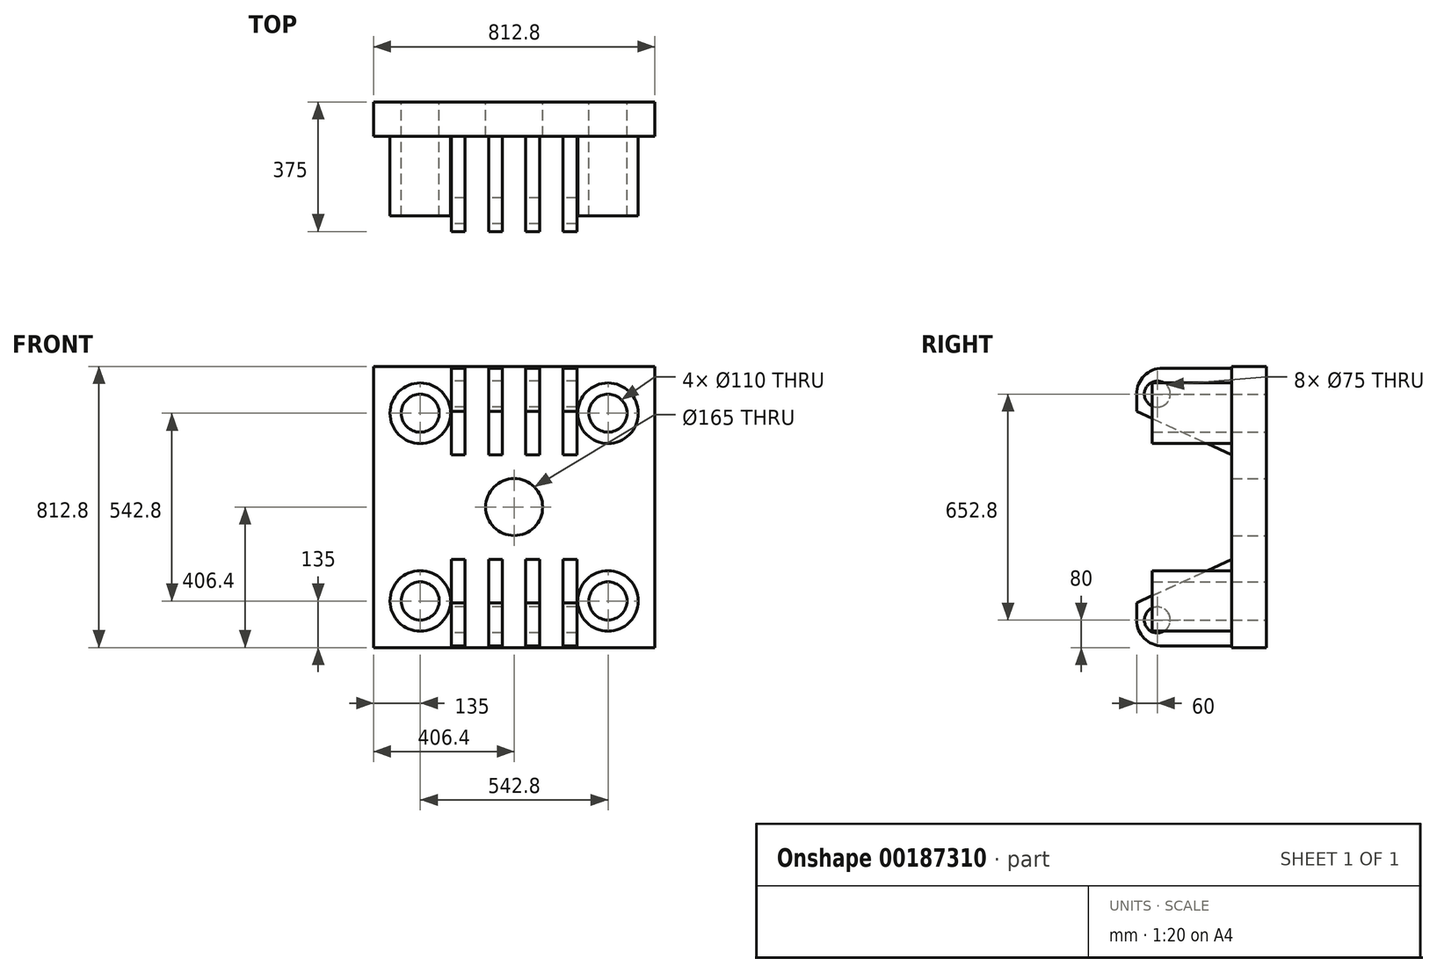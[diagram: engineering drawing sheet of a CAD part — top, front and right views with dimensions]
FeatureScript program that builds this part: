
annotation { "Feature Type Name" : "Feature", "Feature Type Description" : "" }
export const myFeature = defineFeature(function(context is Context, id is Id, definition is map)
    precondition{}
    {
        {
            var Q0;
            Q0=qCreatedBy(makeId("Front.planeOp"),FACE);
            var sketch = newSketch(context, id + "F0", { "sketchPlane" : qUnion([Q0])});
            skLineSegment(sketch, "E0.bottom", {"start": v(-406.4, -406.4) * mm, "end": v(406.4, -406.4) * mm});
            skLineSegment(sketch, "E0.top", {"start": v(-406.4, 406.4) * mm, "end": v(406.4, 406.4) * mm});
            skLineSegment(sketch, "E0.left", {"start": v(-406.4, -406.4) * mm, "end": v(-406.4, 406.4) * mm});
            skLineSegment(sketch, "E0.right", {"start": v(406.4, -406.4) * mm, "end": v(406.4, 406.4) * mm});
            skPoint(sketch, "E0.middle", {"position": v(0, 0) * mm});
            skLineSegment(sketch, "E1", {"start": v(-271.4, 435.08) * mm, "end": v(-271.4, -466.79) * mm, "construction": true});
            skLineSegment(sketch, "E2", {"start": v(271.4, 435.63) * mm, "end": v(271.4, -467.34) * mm, "construction": true});
            skLineSegment(sketch, "E3", {"start": v(-482.99, 271.4) * mm, "end": v(474.5, 271.4) * mm, "construction": true});
            skLineSegment(sketch, "E4", {"start": v(-470.32, -271.4) * mm, "end": v(478.3, -271.4) * mm, "construction": true});
            skCircle(sketch, "E5", {"center": v(-271.4, 271.4) * mm, "radius": 55 * mm});
            skLineSegment(sketch, "E6", {"start": v(-420.18, 0) * mm, "end": v(457.83, 0) * mm, "construction": true});
            skCircle(sketch, "E7.MirrorC", {"center": v(-271.4, -271.4) * mm, "radius": 55 * mm});
            skLineSegment(sketch, "E8", {"start": v(0, 436.93) * mm, "end": v(0, -451.52) * mm, "construction": true});
            skCircle(sketch, "E9.MirrorC", {"center": v(271.4, -271.4) * mm, "radius": 55 * mm});
            skCircle(sketch, "E10.MirrorC", {"center": v(271.4, 271.4) * mm, "radius": 55 * mm});
            skCircle(sketch, "E11", {"center": v(0, 0) * mm, "radius": 82.5 * mm});
            skSolve(sketch);
        }
        {
            var Q0;
            Q0=qSketchRegion(id+"F0",true);
            extrude(context, id + "F1", {"entities" : qUnion([Q0]), "depth" : 100 * mm});
        }
        {
            var Q0;
            Q0=makeQuery(id+"F1.opExtrude","CAP_FACE",FACE,{"disambiguationData":[OSD([sQuery(id+"F0.wireOp",EDGE,"E0.bottom"),sQuery(id+"F0.wireOp",EDGE,"E0.top"),sQuery(id+"F0.wireOp",EDGE,"E0.left"),sQuery(id+"F0.wireOp",EDGE,"E0.right"),sQuery(id+"F0.wireOp",EDGE,"E5"),sQuery(id+"F0.wireOp",EDGE,"E7.MirrorC"),sQuery(id+"F0.wireOp",EDGE,"E9.MirrorC"),sQuery(id+"F0.wireOp",EDGE,"E10.MirrorC"),sQuery(id+"F0.wireOp",EDGE,"E11")])],"isStart":false});
            var sketch = newSketch(context, id + "F2", { "sketchPlane" : qUnion([Q0])});
            skCircle(sketch, "E12", {"center": v(-271.4, 271.4) * mm, "radius": 87.5 * mm});
            skCircle(sketch, "E13", {"center": v(-271.4, 271.4) * mm, "radius": 55 * mm});
            skCircle(sketch, "E14", {"center": v(271.4, 271.4) * mm, "radius": 87.5 * mm});
            skCircle(sketch, "E15", {"center": v(271.4, 271.4) * mm, "radius": 55 * mm});
            skCircle(sketch, "E16", {"center": v(271.4, -271.4) * mm, "radius": 87.5 * mm});
            skCircle(sketch, "E17", {"center": v(271.4, -271.4) * mm, "radius": 55 * mm});
            skCircle(sketch, "E18", {"center": v(-271.4, -271.4) * mm, "radius": 87.5 * mm});
            skCircle(sketch, "E19", {"center": v(-271.4, -271.4) * mm, "radius": 55 * mm});
            skSolve(sketch);
        }
        {
            var Q0;
            Q0 = qSketchRegion(id + "F2", true);
            extrude(context, id + "F3", {"entities" : qUnion([Q0]), "operationType" : NewBodyOperationType.ADD, "depth" : 230 * mm});
        }
        {
            var Q0;
            Q0=makeQuery(id+"FbqTgrZJ77ltsDz_1.opFillet","SPLIT",FACE,{"disambiguationData":[OD(4.0)],"derivedFrom":makeQuery(id+"F1.opExtrude","CAP_FACE",FACE,{"disambiguationData":[OSD([sQuery(id+"F0.wireOp",EDGE,"E0.bottom"),sQuery(id+"F0.wireOp",EDGE,"E0.top"),sQuery(id+"F0.wireOp",EDGE,"E0.left"),sQuery(id+"F0.wireOp",EDGE,"E0.right"),sQuery(id+"F0.wireOp",EDGE,"E5"),sQuery(id+"F0.wireOp",EDGE,"E7.MirrorC"),sQuery(id+"F0.wireOp",EDGE,"E9.MirrorC"),sQuery(id+"F0.wireOp",EDGE,"E10.MirrorC"),sQuery(id+"F0.wireOp",EDGE,"E11")])],"isStart":false})});
            var sketch = newSketch(context, id + "F4", { "sketchPlane" : qUnion([Q0])});
            skLineSegment(sketch, "E20.bottom", {"start": v(-73.8, 401.4) * mm, "end": v(-33.8, 401.4) * mm});
            skLineSegment(sketch, "E20.top", {"start": v(-73.8, 151.4) * mm, "end": v(-33.8, 151.4) * mm});
            skLineSegment(sketch, "E20.left", {"start": v(-73.8, 401.4) * mm, "end": v(-73.8, 151.4) * mm});
            skLineSegment(sketch, "E20.right", {"start": v(-33.8, 401.4) * mm, "end": v(-33.8, 151.4) * mm});
            skLineSegment(sketch, "E21.bottom", {"start": v(33.8, 401.4) * mm, "end": v(73.8, 401.4) * mm});
            skLineSegment(sketch, "E21.top", {"start": v(33.8, 151.4) * mm, "end": v(73.8, 151.4) * mm});
            skLineSegment(sketch, "E21.left", {"start": v(33.8, 401.4) * mm, "end": v(33.8, 151.4) * mm});
            skLineSegment(sketch, "E21.right", {"start": v(73.8, 401.4) * mm, "end": v(73.8, 151.4) * mm});
            skLineSegment(sketch, "E22.bottom", {"start": v(141.4, 401.4) * mm, "end": v(181.4, 401.4) * mm});
            skLineSegment(sketch, "E22.top", {"start": v(141.4, 151.4) * mm, "end": v(181.4, 151.4) * mm});
            skLineSegment(sketch, "E22.left", {"start": v(141.4, 401.4) * mm, "end": v(141.4, 151.4) * mm});
            skLineSegment(sketch, "E22.right", {"start": v(181.4, 401.4) * mm, "end": v(181.4, 151.4) * mm});
            skLineSegment(sketch, "E23", {"start": v(33.8, 401.4) * mm, "end": v(-33.8, 401.4) * mm, "construction": true});
            skLineSegment(sketch, "E24", {"start": v(73.8, 401.4) * mm, "end": v(141.4, 401.4) * mm, "construction": true});
            skLineSegment(sketch, "E25", {"start": v(-406.4, 0) * mm, "end": v(406.4, 0) * mm, "construction": true});
            skLineSegment(sketch, "E26.MirrorCS", {"start": v(141.4, -401.4) * mm, "end": v(181.4, -401.4) * mm});
            skLineSegment(sketch, "E27.MirrorCS", {"start": v(33.8, -401.4) * mm, "end": v(73.8, -401.4) * mm});
            skLineSegment(sketch, "E28.MirrorCS", {"start": v(-73.8, -401.4) * mm, "end": v(-33.8, -401.4) * mm});
            skLineSegment(sketch, "E29.MirrorCS", {"start": v(-73.8, -151.4) * mm, "end": v(-33.8, -151.4) * mm});
            skLineSegment(sketch, "E30.MirrorCS", {"start": v(141.4, -401.4) * mm, "end": v(141.4, -151.4) * mm});
            skLineSegment(sketch, "E31.MirrorCS", {"start": v(141.4, -151.4) * mm, "end": v(181.4, -151.4) * mm});
            skLineSegment(sketch, "E32.MirrorCS", {"start": v(73.8, -401.4) * mm, "end": v(73.8, -151.4) * mm});
            skLineSegment(sketch, "E33.MirrorCS", {"start": v(33.8, -401.4) * mm, "end": v(33.8, -151.4) * mm});
            skLineSegment(sketch, "E34.MirrorCS", {"start": v(181.4, -401.4) * mm, "end": v(181.4, -151.4) * mm});
            skLineSegment(sketch, "E35.MirrorCS", {"start": v(33.8, -151.4) * mm, "end": v(73.8, -151.4) * mm});
            skLineSegment(sketch, "E36.MirrorCS", {"start": v(-33.8, -401.4) * mm, "end": v(-33.8, -151.4) * mm});
            skLineSegment(sketch, "E37.MirrorCS", {"start": v(-73.8, -401.4) * mm, "end": v(-73.8, -151.4) * mm});
            skLineSegment(sketch, "E38.bottom", {"start": v(-181.4, 401.4) * mm, "end": v(-141.4, 401.4) * mm});
            skLineSegment(sketch, "E38.top", {"start": v(-181.4, 151.4) * mm, "end": v(-141.4, 151.4) * mm});
            skLineSegment(sketch, "E38.left", {"start": v(-181.4, 401.4) * mm, "end": v(-181.4, 151.4) * mm});
            skLineSegment(sketch, "E38.right", {"start": v(-141.4, 401.4) * mm, "end": v(-141.4, 151.4) * mm});
            skLineSegment(sketch, "E39", {"start": v(-73.8, 401.4) * mm, "end": v(-141.4, 401.4) * mm, "construction": true});
            skLineSegment(sketch, "E40.MirrorCS", {"start": v(-181.4, -401.4) * mm, "end": v(-141.4, -401.4) * mm});
            skLineSegment(sketch, "E41.MirrorCS", {"start": v(-181.4, -401.4) * mm, "end": v(-181.4, -151.4) * mm});
            skLineSegment(sketch, "E42.MirrorCS", {"start": v(-141.4, -401.4) * mm, "end": v(-141.4, -151.4) * mm});
            skLineSegment(sketch, "E43.MirrorCS", {"start": v(-181.4, -151.4) * mm, "end": v(-141.4, -151.4) * mm});
            skSolve(sketch);
        }
        {
            var Q0;
            Q0 = qSketchRegion(id + "F4", true);
            extrude(context, id + "F5", {"entities" : qUnion([Q0]), "operationType" : NewBodyOperationType.ADD, "depth" : 275 * mm});
        }
        {
            var Q0;
            Q0=makeQuery(id+"F5.opExtrude","SWEPT_FACE",FACE,{"disambiguationData":[OSD([sQuery(id+"F4.wireOp",EDGE,"E38.left")])]});
            var sketch = newSketch(context, id + "F6", { "sketchPlane" : qUnion([Q0])});
            skLineSegment(sketch, "E44", {"start": v(375, 276.4) * mm, "end": v(100, 151.4) * mm});
            skLineSegment(sketch, "E45", {"start": v(100, 151.4) * mm, "end": v(375, 151.4) * mm});
            skLineSegment(sketch, "E46", {"start": v(375, 151.4) * mm, "end": v(375, 276.4) * mm});
            skLineSegment(sketch, "E47", {"start": v(-96.66, 0) * mm, "end": v(488.13, 0) * mm, "construction": true});
            skLineSegment(sketch, "E48.MirrorCS", {"start": v(100, -151.4) * mm, "end": v(375, -151.4) * mm});
            skLineSegment(sketch, "E49.MirrorCS", {"start": v(375, -151.4) * mm, "end": v(375, -276.4) * mm});
            skLineSegment(sketch, "E50.MirrorCS", {"start": v(375, -276.4) * mm, "end": v(100, -151.4) * mm});
            skSolve(sketch);
        }
        {
            var Q0;
            Q0 = qSketchRegion(id + "F6", true);
            var Q1;
            Q1=makeQuery(id+"F5.opExtrude","SWEPT_FACE",FACE,{"disambiguationData":[OSD([sQuery(id+"F4.wireOp",EDGE,"E22.right")])]});
            extrude(context, id + "F7", {"entities" : qUnion([Q0]), "operationType" : NewBodyOperationType.REMOVE, "endBound" : BoundingType.UP_TO_SURFACE, "oppositeDirection" : true, "endBoundEntityFace" : qUnion([Q1]), "depth" : 25 * mm});
        }
        {
            var Q0;
            Q0=makeQuery(id+"F5.opExtrude","CAP_EDGE",EDGE,{"disambiguationData":[OSD([sQuery(id+"F4.wireOp",EDGE,"E22.bottom")])],"isStart":false});
            var Q1;
            {var subQ1=sQuery(id+"F4.wireOp",EDGE,"E22.left");var subQ2=sQuery(id+"F6.wireOp",EDGE,"E44");Q1=makeQuery(id+"F7.boolean.opBoolean","COPY",EDGE,{"disambiguationData":[TD([makeQuery(id+"F5.opExtrude","SWEPT_FACE",FACE,{"disambiguationData":[OSD([subQ1])]})])],"derivedFrom":makeQuery(id+"F7.opExtrude","SWEPT_EDGE",EDGE,{"disambiguationData":[OSD([sQuery(id+"F4.wireOp",EDGE,"E38.left"),subQ2,sQuery(id+"F6.wireOp",EDGE,"E46")])]})});}
            var Q2;
            Q2=makeQuery(id+"F5.opExtrude","CAP_EDGE",EDGE,{"disambiguationData":[OSD([sQuery(id+"F4.wireOp",EDGE,"E21.bottom")])],"isStart":false});
            var Q3;
            {var subQ1=sQuery(id+"F4.wireOp",EDGE,"E21.left");var subQ2=sQuery(id+"F6.wireOp",EDGE,"E44");Q3=makeQuery(id+"F7.boolean.opBoolean","COPY",EDGE,{"disambiguationData":[TD([makeQuery(id+"F5.opExtrude","SWEPT_FACE",FACE,{"disambiguationData":[OSD([subQ1])]})])],"derivedFrom":makeQuery(id+"F7.opExtrude","SWEPT_EDGE",EDGE,{"disambiguationData":[OSD([sQuery(id+"F4.wireOp",EDGE,"E38.left"),subQ2,sQuery(id+"F6.wireOp",EDGE,"E46")])]})});}
            var Q4;
            Q4=makeQuery(id+"F5.opExtrude","CAP_EDGE",EDGE,{"disambiguationData":[OSD([sQuery(id+"F4.wireOp",EDGE,"E20.bottom")])],"isStart":false});
            var Q5;
            {var subQ1=sQuery(id+"F4.wireOp",EDGE,"E20.left");var subQ2=sQuery(id+"F6.wireOp",EDGE,"E44");Q5=makeQuery(id+"F7.boolean.opBoolean","COPY",EDGE,{"disambiguationData":[TD([makeQuery(id+"F5.opExtrude","SWEPT_FACE",FACE,{"disambiguationData":[OSD([subQ1])]})])],"derivedFrom":makeQuery(id+"F7.opExtrude","SWEPT_EDGE",EDGE,{"disambiguationData":[OSD([sQuery(id+"F4.wireOp",EDGE,"E38.left"),subQ2,sQuery(id+"F6.wireOp",EDGE,"E46")])]})});}
            var Q6;
            Q6=makeQuery(id+"F5.opExtrude","CAP_EDGE",EDGE,{"disambiguationData":[OSD([sQuery(id+"F4.wireOp",EDGE,"E38.bottom")])],"isStart":false});
            var Q7;
            {var subQ1=sQuery(id+"F4.wireOp",EDGE,"E38.left");var subQ2=sQuery(id+"F6.wireOp",EDGE,"E44");Q7=makeQuery(id+"F7.boolean.opBoolean","COPY",EDGE,{"disambiguationData":[TD([makeQuery(id+"F5.opExtrude","SWEPT_FACE",FACE,{"disambiguationData":[OSD([subQ1])]})])],"derivedFrom":makeQuery(id+"F7.opExtrude","SWEPT_EDGE",EDGE,{"disambiguationData":[OSD([subQ1,subQ2,sQuery(id+"F6.wireOp",EDGE,"E46")])]})});}
            var Q8;
            {var subQ1=sQuery(id+"F4.wireOp",EDGE,"E41.MirrorCS");var subQ2=sQuery(id+"F6.wireOp",EDGE,"E50.MirrorCS");Q8=makeQuery(id+"F7.boolean.opBoolean","COPY",EDGE,{"disambiguationData":[TD([makeQuery(id+"F5.opExtrude","SWEPT_FACE",FACE,{"disambiguationData":[OSD([subQ1])]})])],"derivedFrom":makeQuery(id+"F7.opExtrude","SWEPT_EDGE",EDGE,{"disambiguationData":[OSD([sQuery(id+"F6.wireOp",EDGE,"E49.MirrorCS"),subQ2])]})});}
            var Q9;
            Q9=makeQuery(id+"F5.opExtrude","CAP_EDGE",EDGE,{"disambiguationData":[OSD([sQuery(id+"F4.wireOp",EDGE,"E40.MirrorCS")])],"isStart":false});
            var Q10;
            {var subQ1=sQuery(id+"F4.wireOp",EDGE,"E36.MirrorCS");var subQ2=sQuery(id+"F6.wireOp",EDGE,"E50.MirrorCS");Q10=makeQuery(id+"F7.boolean.opBoolean","COPY",EDGE,{"disambiguationData":[TD([makeQuery(id+"F5.opExtrude","SWEPT_FACE",FACE,{"disambiguationData":[OSD([subQ1])]})])],"derivedFrom":makeQuery(id+"F7.opExtrude","SWEPT_EDGE",EDGE,{"disambiguationData":[OSD([sQuery(id+"F6.wireOp",EDGE,"E49.MirrorCS"),subQ2])]})});}
            var Q11;
            Q11=makeQuery(id+"F5.opExtrude","CAP_EDGE",EDGE,{"disambiguationData":[OSD([sQuery(id+"F4.wireOp",EDGE,"E28.MirrorCS")])],"isStart":false});
            var Q12;
            {var subQ1=sQuery(id+"F4.wireOp",EDGE,"E32.MirrorCS");var subQ2=sQuery(id+"F6.wireOp",EDGE,"E50.MirrorCS");Q12=makeQuery(id+"F7.boolean.opBoolean","COPY",EDGE,{"disambiguationData":[TD([makeQuery(id+"F5.opExtrude","SWEPT_FACE",FACE,{"disambiguationData":[OSD([subQ1])]})])],"derivedFrom":makeQuery(id+"F7.opExtrude","SWEPT_EDGE",EDGE,{"disambiguationData":[OSD([sQuery(id+"F6.wireOp",EDGE,"E49.MirrorCS"),subQ2])]})});}
            var Q13;
            Q13=makeQuery(id+"F5.opExtrude","CAP_EDGE",EDGE,{"disambiguationData":[OSD([sQuery(id+"F4.wireOp",EDGE,"E27.MirrorCS")])],"isStart":false});
            var Q14;
            {var subQ1=sQuery(id+"F4.wireOp",EDGE,"E30.MirrorCS");var subQ2=sQuery(id+"F6.wireOp",EDGE,"E50.MirrorCS");Q14=makeQuery(id+"F7.boolean.opBoolean","COPY",EDGE,{"disambiguationData":[TD([makeQuery(id+"F5.opExtrude","SWEPT_FACE",FACE,{"disambiguationData":[OSD([subQ1])]})])],"derivedFrom":makeQuery(id+"F7.opExtrude","SWEPT_EDGE",EDGE,{"disambiguationData":[OSD([sQuery(id+"F6.wireOp",EDGE,"E49.MirrorCS"),subQ2])]})});}
            var Q15;
            Q15=makeQuery(id+"F5.opExtrude","CAP_EDGE",EDGE,{"disambiguationData":[OSD([sQuery(id+"F4.wireOp",EDGE,"E26.MirrorCS")])],"isStart":false});
            fillet(context, id + "F8", {"entities" : qUnion([Q0, Q1, Q2, Q3, Q4, Q5, Q6, Q7, Q8, Q9, Q10, Q11, Q12, Q13, Q14, Q15]), "radius" : 75 * mm, "tangentPropagation" : true, "allowEdgeOverflow" : false});
        }
        {
            var Q0;
            Q0=makeQuery(id+"F5.opExtrude","SWEPT_FACE",FACE,{"disambiguationData":[OSD([sQuery(id+"F4.wireOp",EDGE,"E38.left")])]});
            var sketch = newSketch(context, id + "F9", { "sketchPlane" : qUnion([Q0])});
            skCircle(sketch, "E51", {"center": v(315, 326.4) * mm, "radius": 37.5 * mm});
            skCircle(sketch, "E52", {"center": v(315, -326.4) * mm, "radius": 37.5 * mm});
            skSolve(sketch);
        }
        {
            var Q0;
            Q0 = qSketchRegion(id + "F9", true);
            var Q1;
            Q1=makeQuery(id+"F5.opExtrude","SWEPT_FACE",FACE,{"disambiguationData":[OSD([sQuery(id+"F4.wireOp",EDGE,"E22.right")])]});
            extrude(context, id + "F10", {"entities" : qUnion([Q0]), "operationType" : NewBodyOperationType.REMOVE, "endBound" : BoundingType.UP_TO_SURFACE, "oppositeDirection" : true, "endBoundEntityFace" : qUnion([Q1]), "depth" : 25 * mm});
        }
    });
